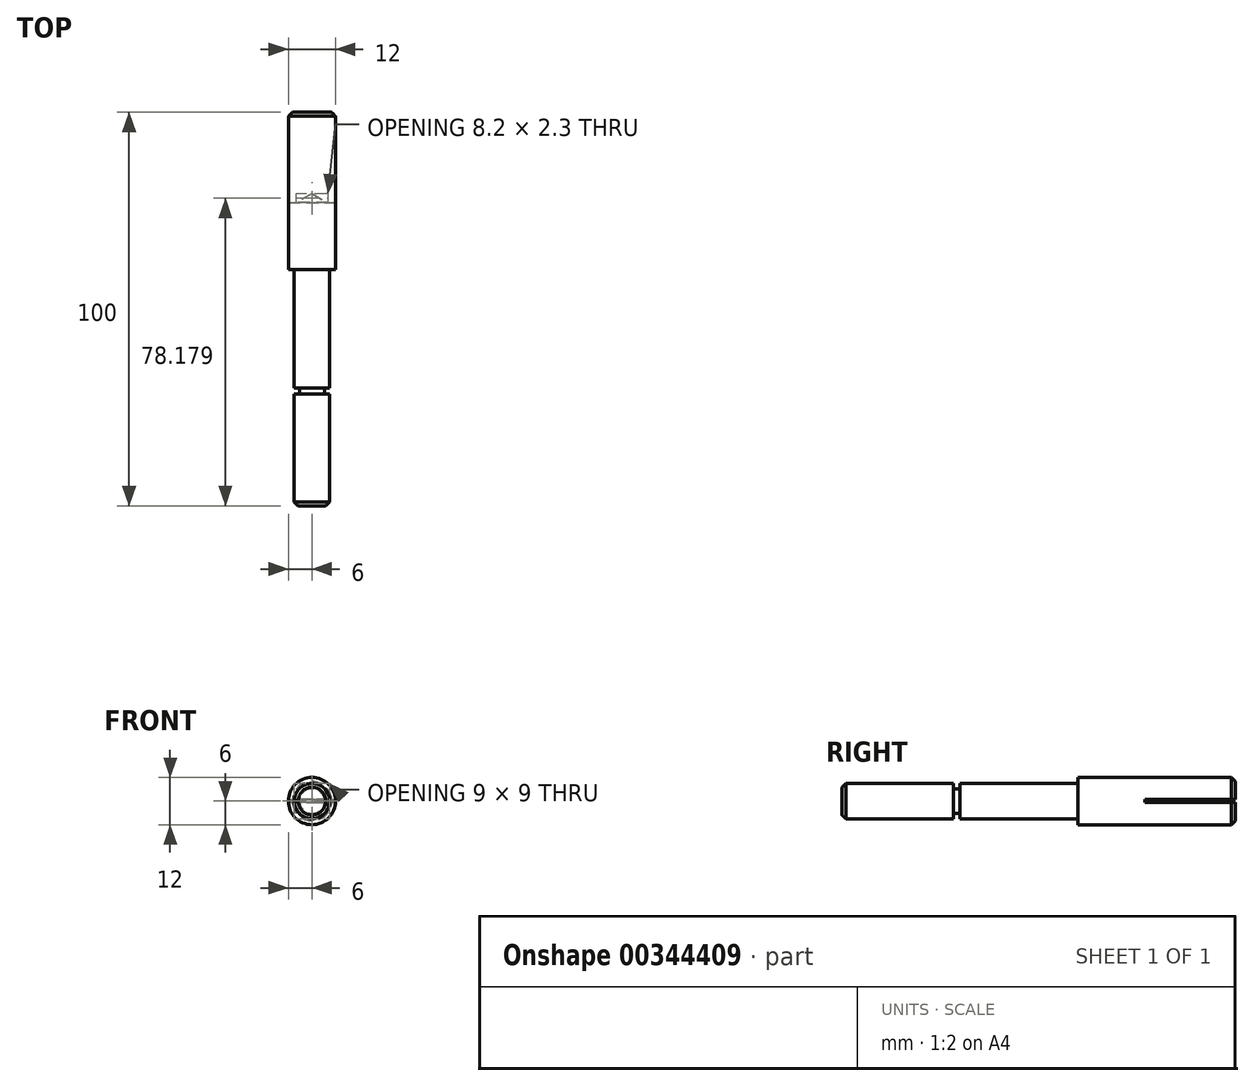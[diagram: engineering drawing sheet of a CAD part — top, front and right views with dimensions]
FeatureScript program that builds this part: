
annotation { "Feature Type Name" : "Feature", "Feature Type Description" : "" }
export const myFeature = defineFeature(function(context is Context, id is Id, definition is map)
    precondition{}
    {
        {
            var Q0;
            Q0=qCreatedBy(makeId("Front.planeOp"),FACE);
            var sketch = newSketch(context, id + "F0", { "sketchPlane" : qUnion([Q0])});
            skCircle(sketch, "E0", {"center": v(0, 0) * mm, "radius": 6 * mm});
            skSolve(sketch);
        }
        {
            var Q0;
            Q0=qCreatedBy(makeId("Front.planeOp"),FACE);
            var sketch = newSketch(context, id + "F1", { "sketchPlane" : qUnion([Q0])});
            skCircle(sketch, "E1", {"center": v(0, 0) * mm, "radius": 4.5 * mm});
            skSolve(sketch);
        }
        {
            var Q0;
            Q0=makeQuery(id+"F0.imprint","IMPRINT",FACE,{"disambiguationData":[TD([[makeQuery(id+"F0.imprint","IMPRINT",EDGE,{"derivedFrom":sQuery(id+"F0.wireOp",EDGE,"E0")}),1.0]])]});
            extrude(context, id + "F2", {"entities" : qUnion([Q0]), "oppositeDirection" : true, "depth" : 40 * mm});
        }
        {
            var Q0;
            Q0=makeQuery(id+"F1.imprint","IMPRINT",FACE,{"disambiguationData":[TD([[makeQuery(id+"F1.imprint","IMPRINT",EDGE,{"derivedFrom":sQuery(id+"F1.wireOp",EDGE,"E1")}),1.0]])]});
            extrude(context, id + "F3", {"entities" : qUnion([Q0]), "operationType" : NewBodyOperationType.ADD, "depth" : 60 * mm});
        }
        {
            var Q0;
            Q0=qCreatedBy(makeId("Right.planeOp"),FACE);
            var sketch = newSketch(context, id + "F4", { "sketchPlane" : qUnion([Q0])});
            skLineSegment(sketch, "E2.bottom", {"start": v(-30, 4.5) * mm, "end": v(-31.6, 4.5) * mm});
            skLineSegment(sketch, "E2.top", {"start": v(-30, 3.15) * mm, "end": v(-31.6, 3.15) * mm});
            skLineSegment(sketch, "E2.left", {"start": v(-30, 4.5) * mm, "end": v(-30, 3.15) * mm});
            skLineSegment(sketch, "E2.right", {"start": v(-31.6, 4.5) * mm, "end": v(-31.6, 3.15) * mm});
            skSolve(sketch);
        }
        {
            var Q0;
            Q0=makeQuery(id+"F4.imprint","IMPRINT",FACE,{"disambiguationData":[TD([[makeQuery(id+"F4.imprint","IMPRINT",EDGE,{"derivedFrom":sQuery(id+"F4.wireOp",EDGE,"E2.bottom")}),1.0]])]});
            var Q1;
            Q1=makeQuery(id+"F3.opExtrude","SWEPT_FACE",FACE,{"disambiguationData":[OSD([sQuery(id+"F1.wireOp",EDGE,"E1")])]});
            revolve(context, id + "F5", {"operationType" : NewBodyOperationType.REMOVE, "entities" : qUnion([Q0]), "axis" : qUnion([Q1]), "revolveType" : RevolveType.FULL, "oppositeDirection" : true});
        }
        {
            var Q0;
            Q0=makeQuery(id+"F3.opExtrude","CAP_EDGE",EDGE,{"disambiguationData":[OSD([sQuery(id+"F1.wireOp",EDGE,"E1")])],"isStart":false});
            chamfer(context, id + "F6", {"entities" : qUnion([Q0]), "width" : 1 * mm, "tangentPropagation" : true});
        }
        {
            var Q0;
            Q0=makeQuery(id+"F2.opExtrude","CAP_EDGE",EDGE,{"disambiguationData":[OSD([sQuery(id+"F0.wireOp",EDGE,"E0")])],"isStart":false});
            chamfer(context, id + "F7", {"entities" : qUnion([Q0]), "width" : 1 * mm, "tangentPropagation" : true});
        }
        {
            var Q0;
            Q0=qCreatedBy(makeId("Right.planeOp"),FACE);
            var sketch = newSketch(context, id + "F8", { "sketchPlane" : qUnion([Q0])});
            skLineSegment(sketch, "E3.bottom", {"start": v(41.01, 0.4) * mm, "end": v(17.01, 0.4) * mm});
            skLineSegment(sketch, "E3.top", {"start": v(41.01, -0.4) * mm, "end": v(17.01, -0.4) * mm});
            skLineSegment(sketch, "E3.left", {"start": v(41.01, 0.4) * mm, "end": v(41.01, -0.4) * mm});
            skLineSegment(sketch, "E3.right", {"start": v(17.01, 0.4) * mm, "end": v(17.01, -0.4) * mm});
            skSolve(sketch);
        }
        {
            var Q0;
            Q0=makeQuery(id+"F8.imprint","IMPRINT",FACE,{"disambiguationData":[TD([[makeQuery(id+"F8.imprint","IMPRINT",EDGE,{"derivedFrom":sQuery(id+"F8.wireOp",EDGE,"E3.bottom")}),1.0]])]});
            extrude(context, id + "F9", {"entities" : qUnion([Q0]), "operationType" : NewBodyOperationType.REMOVE, "endBound" : BoundingType.SYMMETRIC, "oppositeDirection" : true, "depth" : 13.6 * mm});
        }
        {
            var Q0;
            Q0=qCreatedBy(makeId("Right.planeOp"),FACE);
            var sketch = newSketch(context, id + "F10", { "sketchPlane" : qUnion([Q0])});
            skLineSegment(sketch, "E4", {"start": v(17.03, 0) * mm, "end": v(19.85, 0) * mm, "construction": true});
            skSolve(sketch);
        }
        {
            var Q0;
            Q0=qCreatedBy(makeId("Top.planeOp"),FACE);
            var sketch = newSketch(context, id + "F11", { "sketchPlane" : qUnion([Q0])});
            skLineSegment(sketch, "E5", {"start": v(0, 17.03) * mm, "end": v(4.1, 17.03) * mm});
            skLineSegment(sketch, "E6", {"start": v(0, 17.03) * mm, "end": v(-4.1, 17.03) * mm});
            skLineSegment(sketch, "E7", {"start": v(0, 19.33) * mm, "end": v(4.1, 17.03) * mm});
            skLineSegment(sketch, "E8.MirrorCS", {"start": v(0, 19.33) * mm, "end": v(-4.1, 17.03) * mm});
            skSolve(sketch);
        }
        {
            var Q0;
            Q0 = qSketchRegion(id + "F11", true);
            extrude(context, id + "F12", {"entities" : qUnion([Q0]), "operationType" : NewBodyOperationType.ADD, "endBound" : BoundingType.SYMMETRIC, "depth" : 0.8 * mm});
        }
    });
